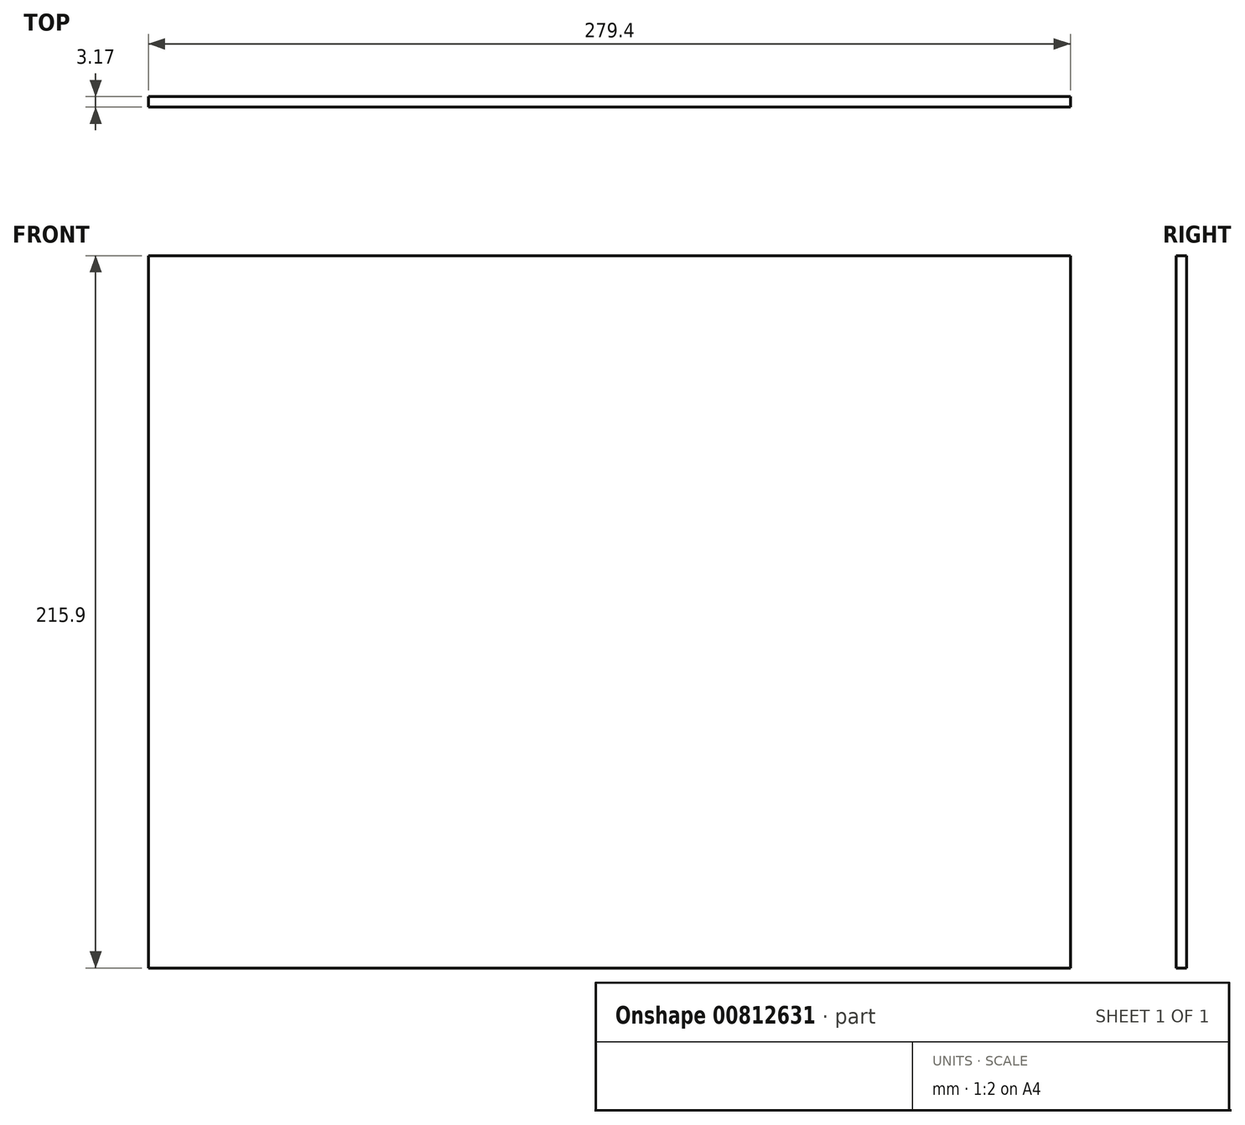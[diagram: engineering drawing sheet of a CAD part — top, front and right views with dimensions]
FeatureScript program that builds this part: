
annotation { "Feature Type Name" : "Feature", "Feature Type Description" : "" }
export const myFeature = defineFeature(function(context is Context, id is Id, definition is map)
    precondition{}
    {
        {
            var Q0;
            Q0=qCreatedBy(makeId("Front.planeOp"),FACE);
            var sketch = newSketch(context, id + "F0", { "sketchPlane" : qUnion([Q0])});
            skLineSegment(sketch, "E0.bottom", {"start": v(139.7, 107.95) * mm, "end": v(-139.7, 107.95) * mm});
            skLineSegment(sketch, "E0.top", {"start": v(139.7, -107.95) * mm, "end": v(-139.7, -107.95) * mm});
            skLineSegment(sketch, "E0.left", {"start": v(139.7, 107.95) * mm, "end": v(139.7, -107.95) * mm});
            skLineSegment(sketch, "E0.right", {"start": v(-139.7, 107.95) * mm, "end": v(-139.7, -107.95) * mm});
            skPoint(sketch, "E0.middle", {"position": v(0, 0) * mm});
            skSolve(sketch);
        }
        {
            var Q0;
            Q0 = qSketchRegion(id + "F0", true);
            extrude(context, id + "F1", {"entities" : qUnion([Q0]), "depth" : 3.17 * mm, "offsetDistance" : 25.4 * mm});
        }
    });
